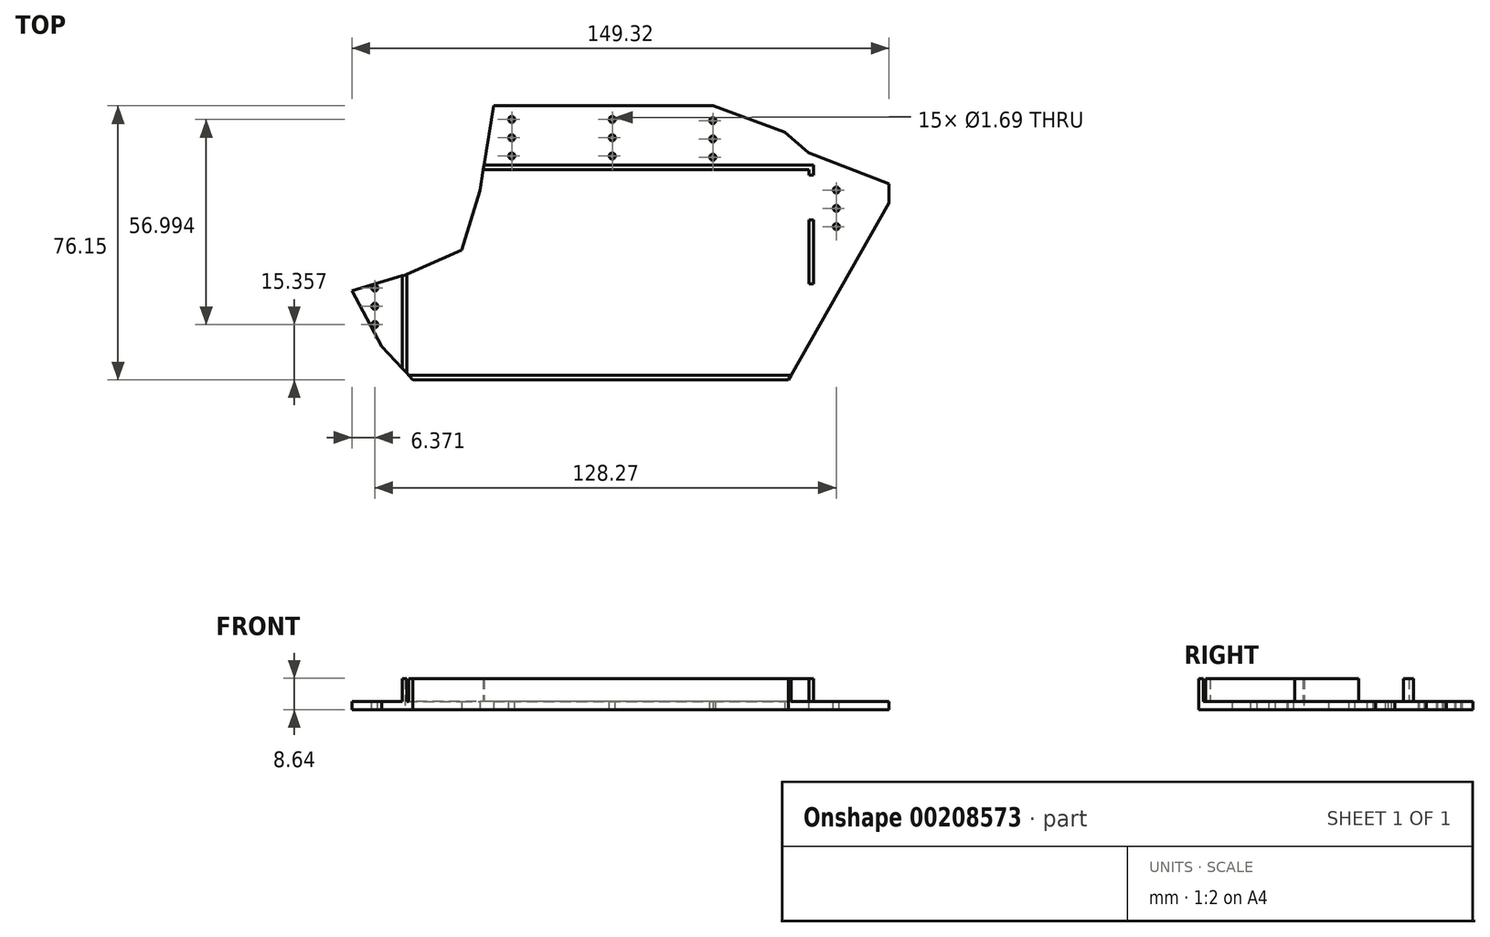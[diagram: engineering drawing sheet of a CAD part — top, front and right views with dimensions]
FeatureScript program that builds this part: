
annotation { "Feature Type Name" : "Feature", "Feature Type Description" : "" }
export const myFeature = defineFeature(function(context is Context, id is Id, definition is map)
    precondition{}
    {
        {
            var Q0;
            Q0=qCreatedBy(makeId("Top.planeOp"),FACE);
            var sketch = newSketch(context, id + "F0", { "sketchPlane" : qUnion([Q0])});
            skLineSegment(sketch, "E0", {"start": v(-31, -29.13) * mm, "end": v(-39.75, -19.88) * mm});
            skLineSegment(sketch, "E1", {"start": v(-39.75, -19.88) * mm, "end": v(-48, -4.38) * mm});
            skLineSegment(sketch, "E2", {"start": v(-48, -4.38) * mm, "end": v(-33.25, 0) * mm});
            skLineSegment(sketch, "E3", {"start": v(-33.25, 0) * mm, "end": v(-17.5, 6.88) * mm});
            skLineSegment(sketch, "E4", {"start": v(-17.5, 6.88) * mm, "end": v(-12.44, 23.38) * mm});
            skLineSegment(sketch, "E5", {"start": v(-12.44, 23.38) * mm, "end": v(-10.46, 47.02) * mm});
            skLineSegment(sketch, "E6", {"start": v(-10.46, 47.02) * mm, "end": v(19.98, 47.02) * mm});
            skLineSegment(sketch, "E7", {"start": v(19.98, 47.02) * mm, "end": v(21.89, 47.02) * mm});
            skLineSegment(sketch, "E8", {"start": v(21.89, 47.02) * mm, "end": v(52.33, 47.02) * mm});
            skLineSegment(sketch, "E9", {"start": v(50.42, 47.02) * mm, "end": v(52.33, 47.02) * mm});
            skLineSegment(sketch, "E10", {"start": v(78.88, 34.03) * mm, "end": v(101.32, 25.34) * mm});
            skLineSegment(sketch, "E11", {"start": v(101.32, 25.34) * mm, "end": v(101.32, 20.06) * mm});
            skLineSegment(sketch, "E12", {"start": v(73.3, -29.13) * mm, "end": v(-31, -29.13) * mm});
            skLineSegment(sketch, "E13", {"start": v(-10.46, 47.02) * mm, "end": v(-10.46, 53.42) * mm});
            skLineSegment(sketch, "E14", {"start": v(-10.46, 53.42) * mm, "end": v(-8.56, 53.42) * mm});
            skLineSegment(sketch, "E15", {"start": v(-8.56, 53.42) * mm, "end": v(-8.56, 47.02) * mm});
            skLineSegment(sketch, "E16", {"start": v(19.98, 47.02) * mm, "end": v(19.98, 53.42) * mm});
            skLineSegment(sketch, "E17", {"start": v(19.98, 53.42) * mm, "end": v(21.89, 53.42) * mm});
            skLineSegment(sketch, "E18", {"start": v(21.89, 53.42) * mm, "end": v(21.89, 47.02) * mm});
            skLineSegment(sketch, "E19", {"start": v(52.33, 47.02) * mm, "end": v(53.46, 53.42) * mm});
            skLineSegment(sketch, "E20", {"start": v(50.42, 53.42) * mm, "end": v(53.46, 53.42) * mm});
            skLineSegment(sketch, "E21", {"start": v(50.42, 53.42) * mm, "end": v(50.42, 47.02) * mm});
            skLineSegment(sketch, "E22", {"start": v(101.32, 25.34) * mm, "end": v(102.22, 27.67) * mm});
            skLineSegment(sketch, "E23", {"start": v(-8.56, 47.02) * mm, "end": v(-12.44, 23.38) * mm});
            skLineSegment(sketch, "E24", {"start": v(101.32, 20.06) * mm, "end": v(73.3, -29.13) * mm});
            skLineSegment(sketch, "E25", {"start": v(52.33, 47.02) * mm, "end": v(72.33, 39.67) * mm});
            skLineSegment(sketch, "E26", {"start": v(102.22, 27.67) * mm, "end": v(103.95, 27) * mm});
            skLineSegment(sketch, "E27", {"start": v(103.95, 27) * mm, "end": v(101.32, 20.06) * mm});
            skLineSegment(sketch, "E28", {"start": v(72.33, 39.67) * mm, "end": v(78.88, 34.03) * mm});
            skSolve(sketch);
        }
        {
            var Q0;
            Q0=makeQuery(id+"F0.imprint","IMPRINT",FACE,{"disambiguationData":[TD([[makeQuery(id+"F0.imprint","IMPRINT",EDGE,{"derivedFrom":sQuery(id+"F0.wireOp",EDGE,"E0")}),-1.0]])]});
            var Q1;
            Q1=makeQuery(id+"F0.imprint","IMPRINT",FACE,{"disambiguationData":[TD([[makeQuery(id+"F0.imprint","IMPRINT",EDGE,{"derivedFrom":sQuery(id+"F0.wireOp",EDGE,"Gi2NU1hI-RyGe-3cBe-QKJR-tDSeOLIxTJu2")}),-1.0]])]});
            extrude(context, id + "F1", {"entities" : qUnion([Q0, Q1]), "depth" : 2.3 * mm});
        }
        {
            var Q0;
            Q0=makeQuery(id+"F1.opExtrude","CAP_FACE",FACE,{"disambiguationData":[OSD([sQuery(id+"F0.wireOp",EDGE,"E0"),sQuery(id+"F0.wireOp",EDGE,"E1"),sQuery(id+"F0.wireOp",EDGE,"E2"),sQuery(id+"F0.wireOp",EDGE,"E3"),sQuery(id+"F0.wireOp",EDGE,"E4"),sQuery(id+"F0.wireOp",EDGE,"E6"),sQuery(id+"F0.wireOp",EDGE,"E7"),sQuery(id+"F0.wireOp",EDGE,"E8"),sQuery(id+"F0.wireOp",EDGE,"E9"),sQuery(id+"F0.wireOp",EDGE,"E10"),sQuery(id+"F0.wireOp",EDGE,"E11"),sQuery(id+"F0.wireOp",EDGE,"E12"),sQuery(id+"F0.wireOp",EDGE,"E23"),sQuery(id+"F0.wireOp",EDGE,"E24"),sQuery(id+"F0.wireOp",EDGE,"E25"),sQuery(id+"F0.wireOp",EDGE,"E28")])],"isStart":false});
            var sketch = newSketch(context, id + "F2", { "sketchPlane" : qUnion([Q0])});
            skPoint(sketch, "E29", {"position": v(-41.63, -3.61) * mm});
            skPoint(sketch, "E30", {"position": v(-41.63, -8.7) * mm});
            skPoint(sketch, "E31", {"position": v(-41.63, -13.77) * mm});
            skLineSegment(sketch, "E32", {"start": v(-34, -29.13) * mm, "end": v(-34, 30.56) * mm});
            skLineSegment(sketch, "E33", {"start": v(-34, 30.56) * mm, "end": v(80.3, 30.56) * mm});
            skLineSegment(sketch, "E34", {"start": v(-32.74, -27.86) * mm, "end": v(79.02, -27.86) * mm});
            skLineSegment(sketch, "E35", {"start": v(-32.74, 29.3) * mm, "end": v(79.02, 29.3) * mm});
            skLineSegment(sketch, "E36", {"start": v(-32.74, 29.3) * mm, "end": v(-32.74, -27.86) * mm});
            skLineSegment(sketch, "E37", {"start": v(79.02, 29.3) * mm, "end": v(79.02, -27.86) * mm});
            skPoint(sketch, "E38.orphan", {"position": v(80.3, 29.3) * mm});
            skPoint(sketch, "E39", {"position": v(-3.55, 43.22) * mm});
            skPoint(sketch, "E40", {"position": v(-3.55, 38.14) * mm});
            skPoint(sketch, "E41", {"position": v(24.39, 43.22) * mm});
            skPoint(sketch, "E42", {"position": v(24.39, 38.14) * mm});
            skPoint(sketch, "E43", {"position": v(24.39, 33.06) * mm});
            skPoint(sketch, "E44", {"position": v(52.33, 42.9) * mm});
            skPoint(sketch, "E45", {"position": v(52.33, 37.82) * mm});
            skPoint(sketch, "E46", {"position": v(52.33, 32.74) * mm});
            skPoint(sketch, "E47", {"position": v(86.64, 23.6) * mm});
            skPoint(sketch, "E48", {"position": v(86.64, 18.52) * mm});
            skPoint(sketch, "E49", {"position": v(86.64, 13.44) * mm});
            skPoint(sketch, "E50", {"position": v(-3.55, 33.06) * mm});
            skLineSegment(sketch, "E51", {"start": v(79.02, 27.7) * mm, "end": v(80.3, 27.7) * mm});
            skLineSegment(sketch, "E52", {"start": v(79.02, 15.32) * mm, "end": v(80.3, 15.32) * mm});
            skLineSegment(sketch, "E53", {"start": v(79.02, -2.46) * mm, "end": v(80.3, -2.46) * mm});
            skLineSegment(sketch, "E54", {"start": v(-34, -29.13) * mm, "end": v(80.3, -29.13) * mm});
            skLineSegment(sketch, "E55", {"start": v(80.3, -29.13) * mm, "end": v(80.3, 27.7) * mm});
            skLineSegment(sketch, "E56", {"start": v(80.3, 30.56) * mm, "end": v(80.3, 27.7) * mm});
            skLineSegment(sketch, "E57", {"start": v(79.02, -21.5) * mm, "end": v(80.3, -21.5) * mm});
            skLineSegment(sketch, "E58.left", {"start": v(79.02, 27.7) * mm, "end": v(79.02, 15.32) * mm});
            skLineSegment(sketch, "E58.right", {"start": v(80.3, 27.7) * mm, "end": v(80.3, 15.32) * mm});
            skLineSegment(sketch, "E59.bottom", {"start": v(80.3, -2.46) * mm, "end": v(79.02, -2.46) * mm});
            skLineSegment(sketch, "E59.top", {"start": v(80.3, -21.5) * mm, "end": v(79.02, -21.5) * mm});
            skLineSegment(sketch, "E59.left", {"start": v(80.3, -2.46) * mm, "end": v(80.3, -21.5) * mm});
            skLineSegment(sketch, "E59.right", {"start": v(79.02, -2.46) * mm, "end": v(79.02, -21.5) * mm});
            skLineSegment(sketch, "E60.left", {"start": v(79.02, 15.32) * mm, "end": v(79.02, -2.46) * mm});
            skLineSegment(sketch, "E60.right", {"start": v(80.3, 15.32) * mm, "end": v(80.3, -2.46) * mm});
            skSolve(sketch);
        }
        {
            var Q0;
            Q0=makeQuery(id+"F2.imprint","IMPRINT",FACE,{"disambiguationData":[TD([[makeQuery(id+"F2.imprint","IMPRINT",EDGE,{"derivedFrom":sQuery(id+"F2.wireOp",EDGE,"E52")}),-1.0]])]});
            var Q1;
            {var subQ0=sQuery(id+"F2.wireOp",EDGE,"E34");var subQ1=makeQuery(id+"F1.opExtrude","CAP_EDGE",EDGE,{"disambiguationData":[OSD([sQuery(id+"F0.wireOp",EDGE,"E0")])],"isStart":false});var subQ2=makeQuery(id+"F2.imprint","INTERSECT",VERTEX,{"derivedFrom":[subQ1,subQ0]});Q1=makeQuery(id+"F2.imprint","IMPRINT",FACE,{"disambiguationData":[TD([[makeQuery(id+"F2.imprint","IMPRINT",EDGE,{"disambiguationData":[TD([[subQ2,-1.0]])],"derivedFrom":subQ0}),-1.0]])]});}
            var Q2;
            {var subQ5=sQuery(id+"F2.wireOp",EDGE,"E56");Q2=makeQuery(id+"F2.imprint","IMPRINT",FACE,{"disambiguationData":[TD([[makeQuery(id+"F2.imprint","IMPRINT",EDGE,{"derivedFrom":subQ5}),-1.0]])]});}
            var Q3;
            {var subQ5=sQuery(id+"F2.wireOp",EDGE,"E32");var subQ7=makeQuery(id+"F1.opExtrude","CAP_EDGE",EDGE,{"disambiguationData":[OSD([sQuery(id+"F0.wireOp",EDGE,"E0")])],"isStart":false});var subQ9=makeQuery(id+"F2.imprint","INTERSECT",VERTEX,{"derivedFrom":[subQ7,subQ5]});Q3=makeQuery(id+"F2.imprint","IMPRINT",FACE,{"disambiguationData":[TD([[makeQuery(id+"F2.imprint","IMPRINT",EDGE,{"disambiguationData":[TD([[subQ9,-1.0]])],"derivedFrom":subQ5}),-1.0]])]});}
            extrude(context, id + "F3", {"entities" : qUnion([Q0, Q1, Q2, Q3]), "operationType" : NewBodyOperationType.ADD, "depth" : 6.35 * mm, "hasSecondDirection" : true, "secondDirectionOppositeDirection" : true, "secondDirectionDepth" : 2.3 * mm});
        }
        {
            var Q0;
            Q0=sQuery(id+"F2.wireOp",VERTEX,"E31");
            var Q1;
            Q1=sQuery(id+"F2.wireOp",VERTEX,"E30");
            var Q2;
            Q2=sQuery(id+"F2.wireOp",VERTEX,"E29");
            var Q3;
            Q3=sQuery(id+"F2.wireOp",VERTEX,"E39");
            var Q4;
            Q4=sQuery(id+"F2.wireOp",VERTEX,"E40");
            var Q5;
            Q5=sQuery(id+"F2.wireOp",VERTEX,"E50");
            var Q6;
            Q6=sQuery(id+"F2.wireOp",VERTEX,"E41");
            var Q7;
            Q7=sQuery(id+"F2.wireOp",VERTEX,"E42");
            var Q8;
            Q8=sQuery(id+"F2.wireOp",VERTEX,"E43");
            var Q9;
            Q9=sQuery(id+"F2.wireOp",VERTEX,"E44");
            var Q10;
            Q10=sQuery(id+"F2.wireOp",VERTEX,"E45");
            var Q11;
            Q11=sQuery(id+"F2.wireOp",VERTEX,"E46");
            var Q12;
            Q12=sQuery(id+"F2.wireOp",VERTEX,"E47");
            var Q13;
            Q13=sQuery(id+"F2.wireOp",VERTEX,"E48");
            var Q14;
            Q14=sQuery(id+"F2.wireOp",VERTEX,"E49");
            var Q15;
            Q15=makeQuery(id+"F1.opExtrude","SWEPT_BODY",BODY,{"disambiguationData":[OSD([sQuery(id+"F0.wireOp",EDGE,"E0"),sQuery(id+"F0.wireOp",EDGE,"E1"),sQuery(id+"F0.wireOp",EDGE,"E2"),sQuery(id+"F0.wireOp",EDGE,"E3"),sQuery(id+"F0.wireOp",EDGE,"E4"),sQuery(id+"F0.wireOp",EDGE,"E6"),sQuery(id+"F0.wireOp",EDGE,"E7"),sQuery(id+"F0.wireOp",EDGE,"E8"),sQuery(id+"F0.wireOp",EDGE,"E9"),sQuery(id+"F0.wireOp",EDGE,"E10"),sQuery(id+"F0.wireOp",EDGE,"E11"),sQuery(id+"F0.wireOp",EDGE,"E12"),sQuery(id+"F0.wireOp",EDGE,"E23"),sQuery(id+"F0.wireOp",EDGE,"E24"),sQuery(id+"F0.wireOp",EDGE,"E25"),sQuery(id+"F0.wireOp",EDGE,"E28")])]});
            hole(context, id + "F4", {"style" : HoleStyle.SIMPLE, "endStyle" : HoleEndStyle.THROUGH, "holeDiameter" : 1.7 * mm, "locations" : qUnion([Q0, Q1, Q2, Q3, Q4, Q5, Q6, Q7, Q8, Q9, Q10, Q11, Q12, Q13, Q14]), "scope" : qUnion([Q15]), "isTappedThrough" : true});
        }
    });
